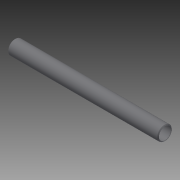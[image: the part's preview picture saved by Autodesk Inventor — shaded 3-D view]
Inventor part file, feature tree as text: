
AUTODESK INVENTOR PART (.ipt)
format: ipt  version: 2013 (Build 170138000, 138)  size: 122,368 bytes
history: native  units: in
note: dims shown in document units (in); Inventor stores cm internally (conversion verified against a paired STEP export)
features: other x42, revolve x1, sketch x1
ambient origin geometry x8: Origin, YZ Plane, XZ Plane, XY Plane, X Axis, Y Axis, Z Axis, Center Point
bodies: Solid1 (feature_tree)
feature tree (44):
  revolve  "Revolution1"  [1 undecoded]
  other  "tube_front_XY"
  other  "tube_front_YZ"
  other  "tube_front_ZX"
  other  "tube_front_X"
  other  "tube_front_Y"
  other  "tube_front_Z"
  other  "tube_front_Center"
  other  "tube_rear_XY"
  other  "tube_rear_YZ"
  other  "tube_rear_ZX"
  other  "tube_rear_X"
  other  "tube_rear_Y"
  other  "tube_rear_Z"
  other  "tube_rear_Center"
  other  "cp1_XY"
  other  "cp1_YZ"
  other  "cp1_ZX"
  other  "cp1_X"
  other  "cp1_Y"
  other  "cp1_Z"
  other  "cp1_Center"
  other  "cp2_XY"
  other  "cp2_YZ"
  other  "cp2_ZX"
  other  "cp2_X"
  other  "cp2_Y"
  other  "cp2_Z"
  other  "cp2_Center"
  other  "cp3_XY"
  other  "cp3_YZ"
  other  "cp3_ZX"
  other  "cp3_X"
  other  "cp3_Y"
  other  "cp3_Z"
  other  "cp3_Center"
  other  "cp4_XY"
  other  "cp4_YZ"
  other  "cp4_ZX"
  other  "cp4_X"
  other  "cp4_Y"
  other  "cp4_Z"
  other  "cp4_Center"
  sketch  "Sketch_1"  dims[d0=360.0deg]
note: 1 required parameter value undecoded (feature->parameter linkage not recoverable at this tier; creation-order binding heuristic only, values carry confidence <= 0.55)
